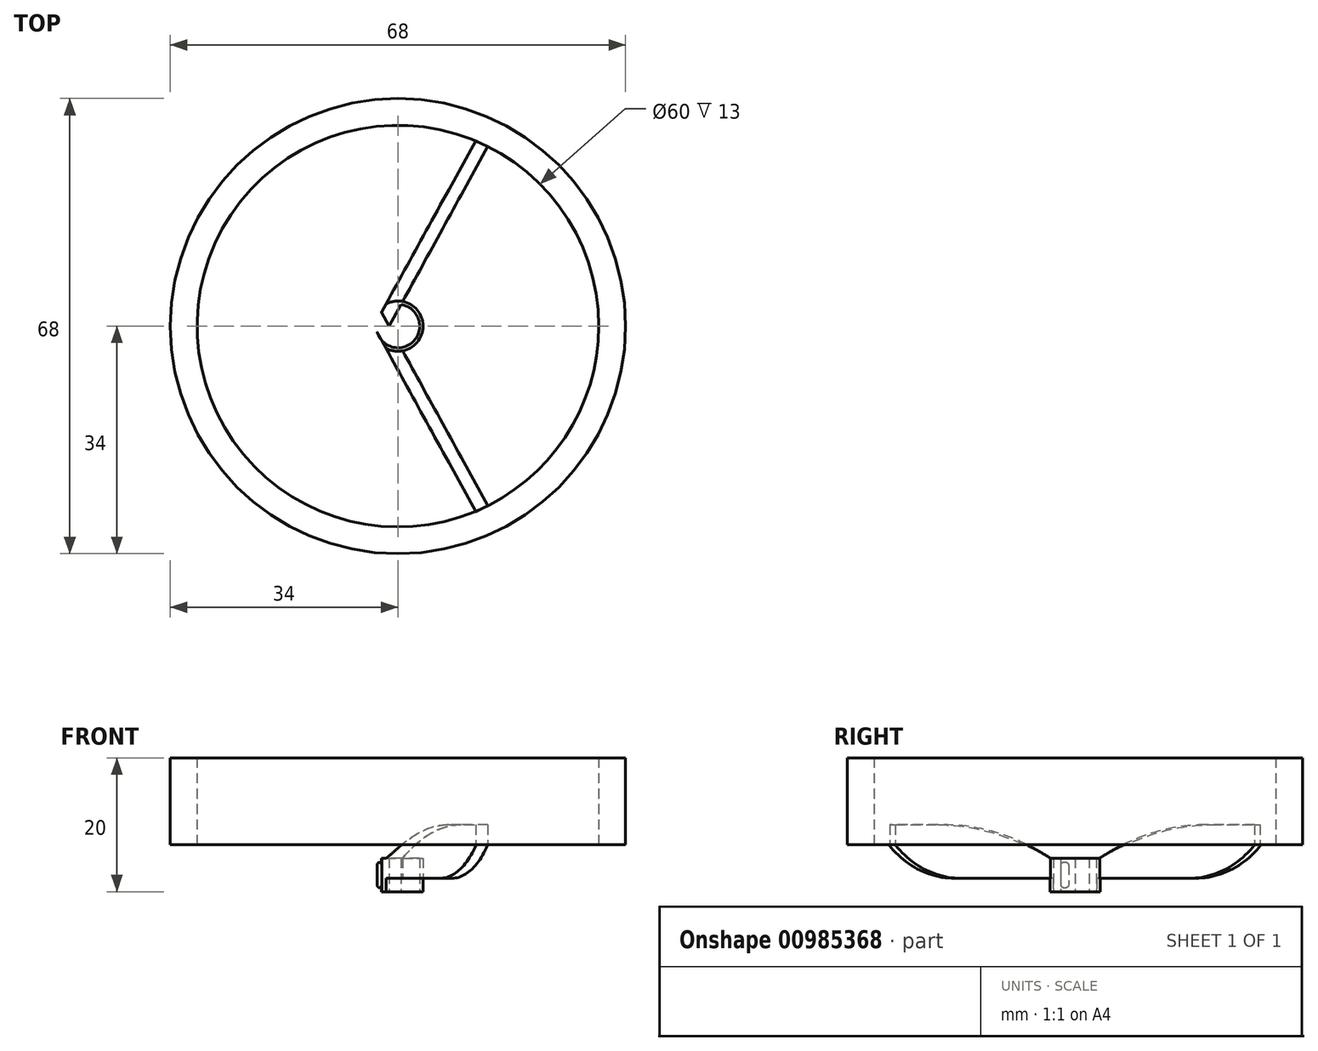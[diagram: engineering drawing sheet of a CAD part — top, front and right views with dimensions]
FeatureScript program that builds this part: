
annotation { "Feature Type Name" : "Feature", "Feature Type Description" : "" }
export const myFeature = defineFeature(function(context is Context, id is Id, definition is map)
    precondition{}
    {
        {
            var Q0;
            Q0=qCreatedBy(makeId("Top.planeOp"),FACE);
            var sketch = newSketch(context, id + "F0", { "sketchPlane" : qUnion([Q0])});
            skCircle(sketch, "E0", {"center": v(0, 0) * mm, "radius": 3.75 * mm});
            skCircle(sketch, "E1", {"center": v(0, 0) * mm, "radius": 3.24 * mm});
            skLineSegment(sketch, "E2", {"start": v(-3.1, 0.91) * mm, "end": v(11.67, 27.8) * mm});
            skLineSegment(sketch, "E3", {"start": v(11.67, 27.8) * mm, "end": v(13.42, 26.83) * mm});
            skLineSegment(sketch, "E4", {"start": v(13.42, 26.83) * mm, "end": v(-2.47, -2.09) * mm});
            skLineSegment(sketch, "E5.MirrorCS", {"start": v(13.42, -26.83) * mm, "end": v(-2.47, 2.09) * mm});
            skLineSegment(sketch, "E6.MirrorCS", {"start": v(-3.1, -0.91) * mm, "end": v(11.67, -27.8) * mm});
            skLineSegment(sketch, "E7.MirrorCS", {"start": v(11.67, -27.8) * mm, "end": v(13.42, -26.83) * mm});
            skCircle(sketch, "E8", {"center": v(0, 0) * mm, "radius": 30 * mm});
            skPoint(sketch, "E8.third.point", {"position": v(-25.91, -15.12) * mm});
            skLineSegment(sketch, "E9", {"start": v(11.67, 27.64) * mm, "end": v(11.67, 27.8) * mm});
            skLineSegment(sketch, "E10.MirrorCS", {"start": v(11.67, -27.64) * mm, "end": v(11.67, -27.8) * mm});
            skCircle(sketch, "E11", {"center": v(0, 0) * mm, "radius": 34 * mm});
            skSolve(sketch);
        }
        {
            var Q0;
            {var subQ0=sQuery(id+"F0.wireOp",EDGE,"E4");var subQ1=sQuery(id+"F0.wireOp",EDGE,"E1");var subQ2=makeQuery(id+"F0.imprint","INTERSECT",VERTEX,{"disambiguationData":[OD(0.0)],"derivedFrom":[subQ1,subQ0]});Q0=makeQuery(id+"F0.imprint","IMPRINT",FACE,{"disambiguationData":[TD([[makeQuery(id+"F0.imprint","IMPRINT",EDGE,{"disambiguationData":[TD([[subQ2,-1.0]])],"derivedFrom":subQ1}),1.0]])]});}
            var Q1;
            {var subQ0=sQuery(id+"F0.wireOp",EDGE,"E4");var subQ1=sQuery(id+"F0.wireOp",EDGE,"E1");var subQ2=makeQuery(id+"F0.imprint","INTERSECT",VERTEX,{"disambiguationData":[OD(0.0)],"derivedFrom":[subQ1,subQ0]});Q1=makeQuery(id+"F0.imprint","IMPRINT",FACE,{"disambiguationData":[TD([[makeQuery(id+"F0.imprint","IMPRINT",EDGE,{"disambiguationData":[TD([[subQ2,1.0]])],"derivedFrom":subQ1}),1.0]])]});}
            var Q2;
            {var subQ0=sQuery(id+"F0.wireOp",EDGE,"E2");var subQ1=sQuery(id+"F0.wireOp",EDGE,"E1");var subQ2=makeQuery(id+"F0.imprint","INTERSECT",VERTEX,{"disambiguationData":[OD(0.0)],"derivedFrom":[subQ1,subQ0]});Q2=makeQuery(id+"F0.imprint","IMPRINT",FACE,{"disambiguationData":[TD([[makeQuery(id+"F0.imprint","IMPRINT",EDGE,{"disambiguationData":[TD([[subQ2,1.0]])],"derivedFrom":subQ1}),1.0]])]});}
            var Q3;
            {var subQ0=sQuery(id+"F0.wireOp",EDGE,"E5.MirrorCS");var subQ1=sQuery(id+"F0.wireOp",EDGE,"E1");var subQ2=makeQuery(id+"F0.imprint","INTERSECT",VERTEX,{"disambiguationData":[OD(0.0)],"derivedFrom":[subQ1,subQ0]});Q3=makeQuery(id+"F0.imprint","IMPRINT",FACE,{"disambiguationData":[TD([[makeQuery(id+"F0.imprint","IMPRINT",EDGE,{"disambiguationData":[TD([[subQ2,1.0]])],"derivedFrom":subQ1}),1.0]])]});}
            var Q4;
            {var subQ0=sQuery(id+"F0.wireOp",EDGE,"E4");var subQ1=sQuery(id+"F0.wireOp",EDGE,"E0");var subQ2=makeQuery(id+"F0.imprint","INTERSECT",VERTEX,{"derivedFrom":[subQ1,subQ0]});Q4=makeQuery(id+"F0.imprint","IMPRINT",FACE,{"disambiguationData":[TD([[makeQuery(id+"F0.imprint","IMPRINT",EDGE,{"disambiguationData":[TD([[subQ2,1.0]])],"derivedFrom":subQ1}),1.0]])]});}
            var Q5;
            {var subQ0=sQuery(id+"F0.wireOp",EDGE,"E2");var subQ1=sQuery(id+"F0.wireOp",EDGE,"E0");var subQ2=makeQuery(id+"F0.imprint","INTERSECT",VERTEX,{"derivedFrom":[subQ1,subQ0]});Q5=makeQuery(id+"F0.imprint","IMPRINT",FACE,{"disambiguationData":[TD([[makeQuery(id+"F0.imprint","IMPRINT",EDGE,{"disambiguationData":[TD([[subQ2,1.0]])],"derivedFrom":subQ1}),1.0]])]});}
            var Q6;
            {var subQ0=sQuery(id+"F0.wireOp",EDGE,"E6.MirrorCS");var subQ1=sQuery(id+"F0.wireOp",EDGE,"E0");var subQ2=makeQuery(id+"F0.imprint","INTERSECT",VERTEX,{"derivedFrom":[subQ1,subQ0]});Q6=makeQuery(id+"F0.imprint","IMPRINT",FACE,{"disambiguationData":[TD([[makeQuery(id+"F0.imprint","IMPRINT",EDGE,{"disambiguationData":[TD([[subQ2,-1.0]])],"derivedFrom":subQ1}),1.0]])]});}
            extrude(context, id + "F1", {"entities" : qUnion([Q0, Q1, Q2, Q3, Q4, Q5, Q6]), "depth" : 5 * mm, "offsetDistance" : 25 * mm});
        }
        {
            var Q0;
            {var subQ4=sQuery(id+"F0.wireOp",EDGE,"E2");Q0=makeQuery(id+"F0.imprint","IMPRINT",FACE,{"disambiguationData":[TD([[makeQuery(id+"F0.imprint","IMPRINT",EDGE,{"derivedFrom":subQ4}),-1.0]])]});}
            var Q1;
            {var subQ4=sQuery(id+"F0.wireOp",EDGE,"E0");var subQ6=sQuery(id+"F0.wireOp",EDGE,"E2");var subQ7=makeQuery(id+"F0.imprint","INTERSECT",VERTEX,{"derivedFrom":[subQ4,subQ6]});Q1=makeQuery(id+"F0.imprint","IMPRINT",FACE,{"disambiguationData":[TD([[makeQuery(id+"F0.imprint","IMPRINT",EDGE,{"disambiguationData":[TD([[subQ7,1.0]])],"derivedFrom":subQ4}),-1.0]])]});}
            var Q2;
            {var subQ0=sQuery(id+"F0.wireOp",EDGE,"E6.MirrorCS");var subQ1=sQuery(id+"F0.wireOp",EDGE,"E0");var subQ2=makeQuery(id+"F0.imprint","INTERSECT",VERTEX,{"derivedFrom":[subQ1,subQ0]});Q2=makeQuery(id+"F0.imprint","IMPRINT",FACE,{"disambiguationData":[TD([[makeQuery(id+"F0.imprint","IMPRINT",EDGE,{"disambiguationData":[TD([[subQ2,-1.0]])],"derivedFrom":subQ1}),-1.0]])]});}
            var Q3;
            {var subQ0=sQuery(id+"F0.wireOp",EDGE,"E7.MirrorCS");Q3=makeQuery(id+"F0.imprint","IMPRINT",FACE,{"disambiguationData":[TD([[makeQuery(id+"F0.imprint","IMPRINT",EDGE,{"derivedFrom":subQ0}),1.0]])]});}
            var Q4;
            {var subQ0=sQuery(id+"F0.wireOp",EDGE,"E3");Q4=makeQuery(id+"F0.imprint","IMPRINT",FACE,{"disambiguationData":[TD([[makeQuery(id+"F0.imprint","IMPRINT",EDGE,{"derivedFrom":subQ0}),-1.0]])]});}
            var Q5;
            {var subQ0=sQuery(id+"F0.wireOp",EDGE,"E10.MirrorCS");Q5=makeQuery(id+"F0.imprint","IMPRINT",FACE,{"disambiguationData":[TD([[makeQuery(id+"F0.imprint","IMPRINT",EDGE,{"derivedFrom":subQ0}),-1.0]])]});}
            extrude(context, id + "F2", {"entities" : qUnion([Q0, Q1, Q2, Q3, Q4, Q5]), "operationType" : NewBodyOperationType.ADD, "depth" : 10 * mm, "offsetDistance" : 25 * mm, "hasSecondDirection" : true, "secondDirectionOppositeDirection" : false, "secondDirectionDepth" : 2 * mm});
        }
        {
            var Q0;
            {var subQ4=sQuery(id+"F0.wireOp",EDGE,"E3");Q0=makeQuery(id+"F0.imprint","IMPRINT",FACE,{"disambiguationData":[TD([[makeQuery(id+"F0.imprint","IMPRINT",EDGE,{"derivedFrom":subQ4}),1.0]])]});}
            var Q1;
            {var subQ0=sQuery(id+"F0.wireOp",EDGE,"E7.MirrorCS");Q1=makeQuery(id+"F0.imprint","IMPRINT",FACE,{"disambiguationData":[TD([[makeQuery(id+"F0.imprint","IMPRINT",EDGE,{"derivedFrom":subQ0}),1.0]])]});}
            var Q2;
            {var subQ0=sQuery(id+"F0.wireOp",EDGE,"E10.MirrorCS");Q2=makeQuery(id+"F0.imprint","IMPRINT",FACE,{"disambiguationData":[TD([[makeQuery(id+"F0.imprint","IMPRINT",EDGE,{"derivedFrom":subQ0}),-1.0]])]});}
            var Q3;
            {var subQ0=sQuery(id+"F0.wireOp",EDGE,"E3");Q3=makeQuery(id+"F0.imprint","IMPRINT",FACE,{"disambiguationData":[TD([[makeQuery(id+"F0.imprint","IMPRINT",EDGE,{"derivedFrom":subQ0}),-1.0]])]});}
            var Q4;
            {var subQ0=sQuery(id+"F0.wireOp",EDGE,"E9");Q4=makeQuery(id+"F0.imprint","IMPRINT",FACE,{"disambiguationData":[TD([[makeQuery(id+"F0.imprint","IMPRINT",EDGE,{"derivedFrom":subQ0}),1.0]])]});}
            extrude(context, id + "F3", {"entities" : qUnion([Q0, Q1, Q2, Q3, Q4]), "operationType" : NewBodyOperationType.ADD, "depth" : 20 * mm, "offsetDistance" : 25 * mm, "hasSecondDirection" : true, "secondDirectionOppositeDirection" : false, "secondDirectionDepth" : 7 * mm});
        }
        {
            var Q0;
            Q0=makeQuery(id+"F3.opExtrude","CAP_EDGE",EDGE,{"disambiguationData":[OSD([sQuery(id+"F0.wireOp",EDGE,"E11")])],"isStart":false});
            var Q1;
            Q1=makeQuery(id+"F3.opExtrude","CAP_EDGE",EDGE,{"disambiguationData":[OSD([sQuery(id+"F0.wireOp",EDGE,"E8")])],"isStart":false});
            var Q2;
            Q2=makeQuery(id+"F3.opExtrude","CAP_EDGE",EDGE,{"disambiguationData":[OSD([sQuery(id+"F0.wireOp",EDGE,"E11")])],"isStart":true});
            var Q3;
            {var subQ0=sQuery(id+"F0.wireOp",EDGE,"E8");Q3=makeQuery(id+"F3.boolean.opBoolean","SPLIT",EDGE,{"disambiguationData":[TD([makeQuery(id+"F2.opExtrude","SWEPT_FACE",FACE,{"disambiguationData":[OSD([sQuery(id+"F0.wireOp",EDGE,"E2")])]})])],"derivedFrom":makeQuery(id+"F3.opExtrude","CAP_EDGE",EDGE,{"disambiguationData":[OSD([subQ0])],"isStart":true})});}
            var Q4;
            {var subQ0=sQuery(id+"F0.wireOp",EDGE,"E8");Q4=makeQuery(id+"F3.boolean.opBoolean","SPLIT",EDGE,{"disambiguationData":[TD([makeQuery(id+"F2.opExtrude","SWEPT_FACE",FACE,{"disambiguationData":[OSD([sQuery(id+"F0.wireOp",EDGE,"E3")])]})])],"derivedFrom":makeQuery(id+"F3.opExtrude","CAP_EDGE",EDGE,{"disambiguationData":[OSD([subQ0])],"isStart":true})});}
            var Q5;
            Q5=makeQuery(id+"F1.opExtrude","CAP_EDGE",EDGE,{"disambiguationData":[OSD([sQuery(id+"F0.wireOp",EDGE,"E1")])],"isStart":true});
            var Q6;
            Q6=makeQuery(id+"F1.opExtrude","CAP_EDGE",EDGE,{"disambiguationData":[OSD([sQuery(id+"F0.wireOp",EDGE,"E1")])],"isStart":false});
            fillet(context, id + "F4", {"entities" : qUnion([Q0, Q1, Q2, Q3, Q4, Q5, Q6]), "radius" : 1 * mm, "tangentPropagation" : true, "allowEdgeOverflow" : false});
        }
        {
            var Q0;
            Q0=qCreatedBy(makeId("Front.planeOp"),FACE);
            var sketch = newSketch(context, id + "F5", { "sketchPlane" : qUnion([Q0])});
            skLineSegment(sketch, "E12.bottom", {"start": v(-14.5, 16) * mm, "end": v(1.5, 16) * mm});
            skLineSegment(sketch, "E12.top", {"start": v(-14.5, 10) * mm, "end": v(1.5, 10) * mm});
            skLineSegment(sketch, "E12.left", {"start": v(-14.5, 16) * mm, "end": v(-14.5, 10) * mm});
            skLineSegment(sketch, "E12.right", {"start": v(1.5, 16) * mm, "end": v(1.5, 10) * mm});
            skSolve(sketch);
        }
        {
            var Q0;
            Q0=makeQuery(id+"F5.imprint","IMPRINT",FACE,{"disambiguationData":[TD([[makeQuery(id+"F5.imprint","IMPRINT",EDGE,{"derivedFrom":sQuery(id+"F5.wireOp",EDGE,"E12.bottom")}),-1.0]])]});
            extrude(context, id + "F6", {"entities" : qUnion([Q0]), "operationType" : NewBodyOperationType.REMOVE, "oppositeDirection" : true, "depth" : 25 * mm, "offsetDistance" : 25 * mm, "hasSecondDirection" : true, "secondDirectionOppositeDirection" : false, "secondDirectionDepth" : 25 * mm});
        }
        {
            var Q0;
            {var subQ0=sQuery(id+"F0.wireOp",EDGE,"E0");Q0=makeQuery(id+"F2.opExtrude","CAP_EDGE",EDGE,{"disambiguationData":[OSD([subQ0]),TDD([makeQuery(id+"F0.imprint","IMPRINT",EDGE,{"disambiguationData":[TD([[makeQuery(id+"F0.imprint","INTERSECT",VERTEX,{"derivedFrom":[subQ0,sQuery(id+"F0.wireOp",EDGE,"E2")]}),1.0]])],"derivedFrom":subQ0})])],"isStart":false});}
            var Q1;
            {var subQ0=sQuery(id+"F0.wireOp",EDGE,"E0");Q1=makeQuery(id+"F2.opExtrude","CAP_EDGE",EDGE,{"disambiguationData":[OSD([subQ0]),TDD([makeQuery(id+"F0.imprint","IMPRINT",EDGE,{"disambiguationData":[TD([[makeQuery(id+"F0.imprint","INTERSECT",VERTEX,{"derivedFrom":[subQ0,sQuery(id+"F0.wireOp",EDGE,"E6.MirrorCS")]}),-1.0]])],"derivedFrom":subQ0})])],"isStart":false});}
            chamfer(context, id + "F7", {"entities" : qUnion([Q0, Q1]), "width" : 5 * mm, "tangentPropagation" : true});
        }
        {
            var Q0;
            {var subQ0=sQuery(id+"F0.wireOp",EDGE,"E4");var subQ1=sQuery(id+"F0.wireOp",EDGE,"E2");var subQ2=sQuery(id+"F0.wireOp",EDGE,"E0");Q0=makeQuery(id+"F7.opChamfer","BLEND_EDGE",EDGE,{"blendedFrom":[makeQuery(id+"F2.opExtrude","CAP_EDGE",EDGE,{"disambiguationData":[OSD([subQ2]),TDD([makeQuery(id+"F0.imprint","IMPRINT",EDGE,{"disambiguationData":[TD([[makeQuery(id+"F0.imprint","INTERSECT",VERTEX,{"derivedFrom":[subQ2,subQ1]}),1.0]])],"derivedFrom":subQ2})])],"isStart":false}),makeQuery(id+"F2.opExtrude","CAP_FACE",FACE,{"disambiguationData":[OSD([subQ2,subQ1,sQuery(id+"F0.wireOp",EDGE,"E3"),subQ0])],"isStart":false})],"blendedInto":[makeQuery(id+"F2.opExtrude","CAP_FACE",FACE,{"disambiguationData":[OSD([subQ2,subQ1,sQuery(id+"F0.wireOp",EDGE,"E3"),subQ0])],"isStart":false})]});}
            var Q1;
            {var subQ0=sQuery(id+"F0.wireOp",EDGE,"E6.MirrorCS");var subQ1=sQuery(id+"F0.wireOp",EDGE,"E5.MirrorCS");var subQ2=sQuery(id+"F0.wireOp",EDGE,"E0");Q1=makeQuery(id+"F7.opChamfer","BLEND_EDGE",EDGE,{"blendedFrom":[makeQuery(id+"F2.opExtrude","CAP_EDGE",EDGE,{"disambiguationData":[OSD([subQ2]),TDD([makeQuery(id+"F0.imprint","IMPRINT",EDGE,{"disambiguationData":[TD([[makeQuery(id+"F0.imprint","INTERSECT",VERTEX,{"derivedFrom":[subQ2,subQ0]}),-1.0]])],"derivedFrom":subQ2})])],"isStart":false}),makeQuery(id+"F2.opExtrude","CAP_FACE",FACE,{"disambiguationData":[OSD([subQ2,subQ1,subQ0,sQuery(id+"F0.wireOp",EDGE,"E7.MirrorCS")])],"isStart":false})],"blendedInto":[makeQuery(id+"F2.opExtrude","CAP_FACE",FACE,{"disambiguationData":[OSD([subQ2,subQ1,subQ0,sQuery(id+"F0.wireOp",EDGE,"E7.MirrorCS")])],"isStart":false})]});}
            fillet(context, id + "F8", {"entities" : qUnion([Q0, Q1]), "radius" : 35 * mm, "tangentPropagation" : true, "allowEdgeOverflow" : false});
        }
        {
            var Q0;
            Q0=makeQuery(id+"F2.opExtrude","CAP_EDGE",EDGE,{"disambiguationData":[OSD([sQuery(id+"F0.wireOp",EDGE,"E7.MirrorCS")])],"isStart":true});
            var Q1;
            Q1=makeQuery(id+"F2.opExtrude","CAP_EDGE",EDGE,{"disambiguationData":[OSD([sQuery(id+"F0.wireOp",EDGE,"E3")])],"isStart":true});
            fillet(context, id + "F9", {"entities" : qUnion([Q0, Q1]), "radius" : 15 * mm, "tangentPropagation" : true, "allowEdgeOverflow" : false});
        }
    });
